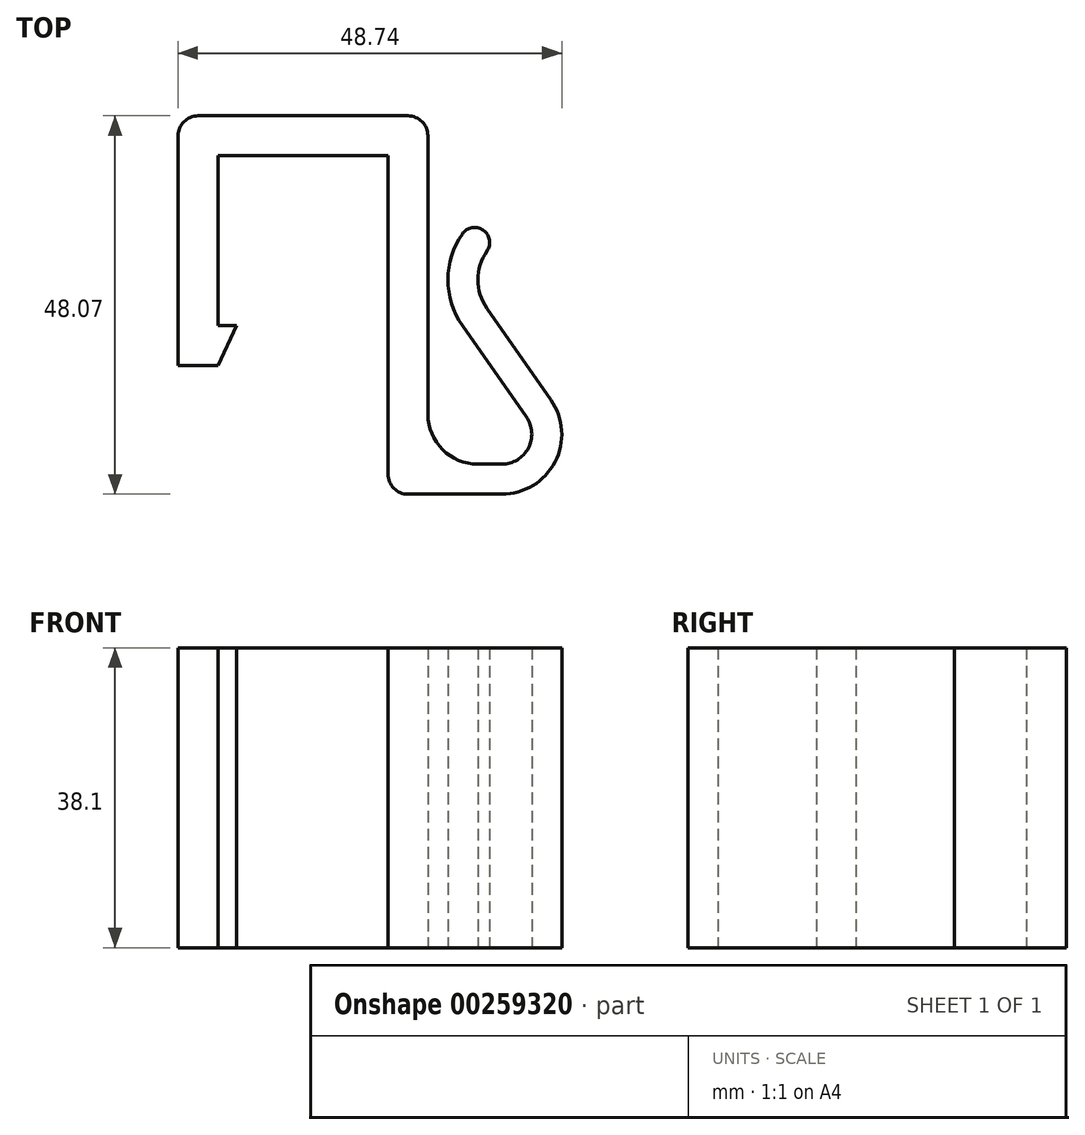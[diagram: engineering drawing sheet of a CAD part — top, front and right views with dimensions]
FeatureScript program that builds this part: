
annotation { "Feature Type Name" : "Feature", "Feature Type Description" : "" }
export const myFeature = defineFeature(function(context is Context, id is Id, definition is map)
    precondition{}
    {
        {
            var Q0;
            Q0=qCreatedBy(makeId("Top.planeOp"),FACE);
            var sketch = newSketch(context, id + "F0", { "sketchPlane" : qUnion([Q0])});
            skLineSegment(sketch, "E0", {"start": v(0, 0) * mm, "end": v(0, 21.59) * mm});
            skLineSegment(sketch, "E1", {"start": v(0, 21.59) * mm, "end": v(21.59, 21.59) * mm});
            skLineSegment(sketch, "E2", {"start": v(21.59, 21.59) * mm, "end": v(21.59, -18.86) * mm});
            skLineSegment(sketch, "E3", {"start": v(24.11, 26.67) * mm, "end": v(-2.54, 26.67) * mm});
            skLineSegment(sketch, "E4", {"start": v(-5.08, 24.13) * mm, "end": v(-5.08, 0) * mm});
            skPoint(sketch, "E5.start.orphan", {"position": v(43.85, 0) * mm});
            skLineSegment(sketch, "E6", {"start": v(24.13, -21.4) * mm, "end": v(36.04, -21.4) * mm});
            skArc(sketch, "E7", {"start": v(36.04, -21.4) * mm, "mid": v(42.8, -17.3) * mm, "end": v(42.28, -9.4) * mm});
            skLineSegment(sketch, "E8", {"start": v(42.28, -9.4) * mm, "end": v(34.15, 2.2) * mm});
            skPoint(sketch, "E8.endSnap0", {"position": v(26.65, 2.2) * mm});
            skArc(sketch, "E9", {"start": v(34.15, 2.2) * mm, "mid": v(33, 5.85) * mm, "end": v(34.15, 9.5) * mm});
            skArc(sketch, "E10", {"start": v(31.03, 11.68) * mm, "mid": v(29.2, 5.85) * mm, "end": v(31.03, 0.02) * mm});
            skLineSegment(sketch, "E11", {"start": v(39.35, 5.85) * mm, "end": v(30.11, 12.32) * mm, "construction": true});
            skLineSegment(sketch, "E12", {"start": v(39.35, 5.85) * mm, "end": v(27.99, -2.1) * mm, "construction": true});
            skArc(sketch, "E13", {"start": v(39.16, -11.59) * mm, "mid": v(39.42, -15.53) * mm, "end": v(36.04, -17.59) * mm});
            skLineSegment(sketch, "E14", {"start": v(36.04, -13.78) * mm, "end": v(47.34, -5.87) * mm, "construction": true});
            skLineSegment(sketch, "E15", {"start": v(39.16, -11.59) * mm, "end": v(31.03, 0.02) * mm});
            skArc(sketch, "E16", {"start": v(34.15, 9.5) * mm, "mid": v(33.68, 12.15) * mm, "end": v(31.03, 11.68) * mm});
            skLineSegment(sketch, "E17", {"start": v(36.04, -17.59) * mm, "end": v(33, -17.59) * mm});
            skLineSegment(sketch, "E18.trimOffspring", {"start": v(26.65, -11.24) * mm, "end": v(26.65, 24.13) * mm});
            skPoint(sketch, "E19.start.orphan", {"position": v(26.65, -22.25) * mm});
            skPoint(sketch, "E20.visualSharp", {"position": v(26.65, -17.59) * mm});
            skArc(sketch, "E20.filletArc", {"start": v(26.65, -11.24) * mm, "mid": v(28.51, -15.73) * mm, "end": v(33, -17.59) * mm});
            skPoint(sketch, "E21.visualSharp", {"position": v(-5.08, 26.67) * mm});
            skArc(sketch, "E21.filletArc", {"start": v(-2.54, 26.67) * mm, "mid": v(-4.34, 25.93) * mm, "end": v(-5.08, 24.13) * mm});
            skPoint(sketch, "E22.visualSharp", {"position": v(26.65, 26.67) * mm});
            skArc(sketch, "E22.filletArc", {"start": v(26.65, 24.13) * mm, "mid": v(25.9, 25.93) * mm, "end": v(24.11, 26.67) * mm});
            skPoint(sketch, "E23.visualSharp", {"position": v(21.59, -21.4) * mm});
            skArc(sketch, "E23.filletArc", {"start": v(21.6, -18.86) * mm, "mid": v(22.33, -20.65) * mm, "end": v(24.13, -21.4) * mm});
            skLineSegment(sketch, "E24", {"start": v(-5.08, 0) * mm, "end": v(-5.08, -5.08) * mm});
            skLineSegment(sketch, "E25", {"start": v(-5.08, -5.08) * mm, "end": v(0, -5.08) * mm});
            skLineSegment(sketch, "E26", {"start": v(0, -5.08) * mm, "end": v(2.37, 0) * mm});
            skLineSegment(sketch, "E27", {"start": v(2.37, 0) * mm, "end": v(0, 0) * mm});
            skSolve(sketch);
        }
        {
            var Q0;
            Q0 = qSketchRegion(id + "F0", true);
            extrude(context, id + "F1", {"entities" : qUnion([Q0]), "depth" : 38.1 * mm});
        }
    });
